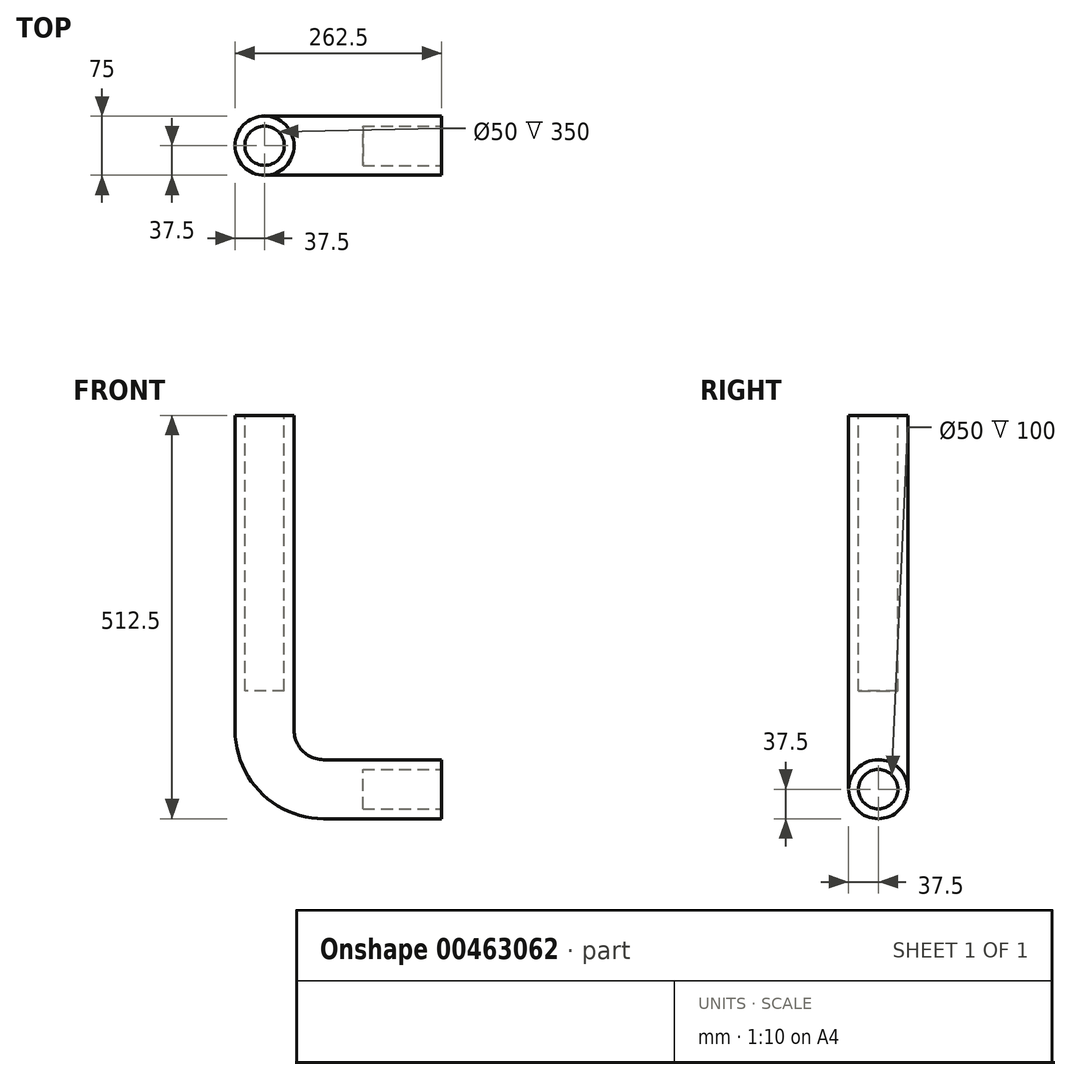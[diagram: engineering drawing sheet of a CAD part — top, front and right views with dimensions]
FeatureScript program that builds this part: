
annotation { "Feature Type Name" : "Feature", "Feature Type Description" : "" }
export const myFeature = defineFeature(function(context is Context, id is Id, definition is map)
    precondition{}
    {
        {
            var Q0;
            Q0=qCreatedBy(makeId("Right.planeOp"),FACE);
            var sketch = newSketch(context, id + "F0", { "sketchPlane" : qUnion([Q0])});
            skCircle(sketch, "E0", {"center": v(0, 0) * mm, "radius": 37.5 * mm});
            skSolve(sketch);
        }
        {
            var Q0;
            Q0=qCreatedBy(makeId("Front.planeOp"),FACE);
            var sketch = newSketch(context, id + "F1", { "sketchPlane" : qUnion([Q0])});
            skLineSegment(sketch, "E1", {"start": v(0, 0) * mm, "end": v(-150, 0) * mm});
            skLineSegment(sketch, "E2", {"start": v(-225, 75) * mm, "end": v(-225, 475) * mm});
            skArc(sketch, "E3", {"start": v(-225, 75) * mm, "mid": v(-203.03, 21.97) * mm, "end": v(-150, 0) * mm});
            skSolve(sketch);
        }
        {
            var Q0;
            Q0=makeQuery(id+"F0.imprint","IMPRINT",FACE,{"disambiguationData":[TD([[makeQuery(id+"F0.imprint","IMPRINT",EDGE,{"derivedFrom":sQuery(id+"F0.wireOp",EDGE,"E0")}),1.0]])]});
            var Q1;
            Q1=sQuery(id+"F1.wireOp",EDGE,"E1");
            var Q2;
            Q2=sQuery(id+"F1.wireOp",EDGE,"E3");
            var Q3;
            Q3=sQuery(id+"F1.wireOp",EDGE,"E2");
            sweep(context, id + "F2", {"profiles" : qUnion([Q0]), "path" : qUnion([Q1, Q2, Q3])});
        }
        {
            var Q0;
            Q0=makeQuery(id+"F2.opSweep","CAP_FACE",FACE,{"disambiguationData":[OSD([sQuery(id+"F0.wireOp",EDGE,"E0"),sQuery(id+"F1.wireOp",VERTEX,"E2.end")])],"isStart":false});
            var sketch = newSketch(context, id + "F3", { "sketchPlane" : qUnion([Q0])});
            skCircle(sketch, "E4", {"center": v(-225, 0) * mm, "radius": 25 * mm});
            skSolve(sketch);
        }
        {
            var Q0;
            Q0=makeQuery(id+"F3.imprint","IMPRINT",FACE,{"disambiguationData":[TD([[makeQuery(id+"F3.imprint","IMPRINT",EDGE,{"derivedFrom":sQuery(id+"F3.wireOp",EDGE,"E4")}),1.0]])]});
            var Q1;
            Q1=sQuery(id+"F3.wireOp",EDGE,"E4");
            extrude(context, id + "F4", {"entities" : qUnion([Q0]), "operationType" : NewBodyOperationType.REMOVE, "surfaceEntities" : qUnion([Q1]), "oppositeDirection" : true, "depth" : 350 * mm});
        }
        {
            var Q0;
            Q0=makeQuery(id+"F2.opSweep","CAP_FACE",FACE,{"disambiguationData":[OSD([sQuery(id+"F0.wireOp",EDGE,"E0"),sQuery(id+"F1.wireOp",VERTEX,"E1.start")])],"isStart":true});
            var sketch = newSketch(context, id + "F5", { "sketchPlane" : qUnion([Q0])});
            skCircle(sketch, "E5", {"center": v(0, 0) * mm, "radius": 25 * mm});
            skSolve(sketch);
        }
        {
            var Q0;
            Q0 = qSketchRegion(id + "F5", true);
            extrude(context, id + "F6", {"entities" : qUnion([Q0]), "operationType" : NewBodyOperationType.REMOVE, "oppositeDirection" : true, "depth" : 100 * mm});
        }
    });
